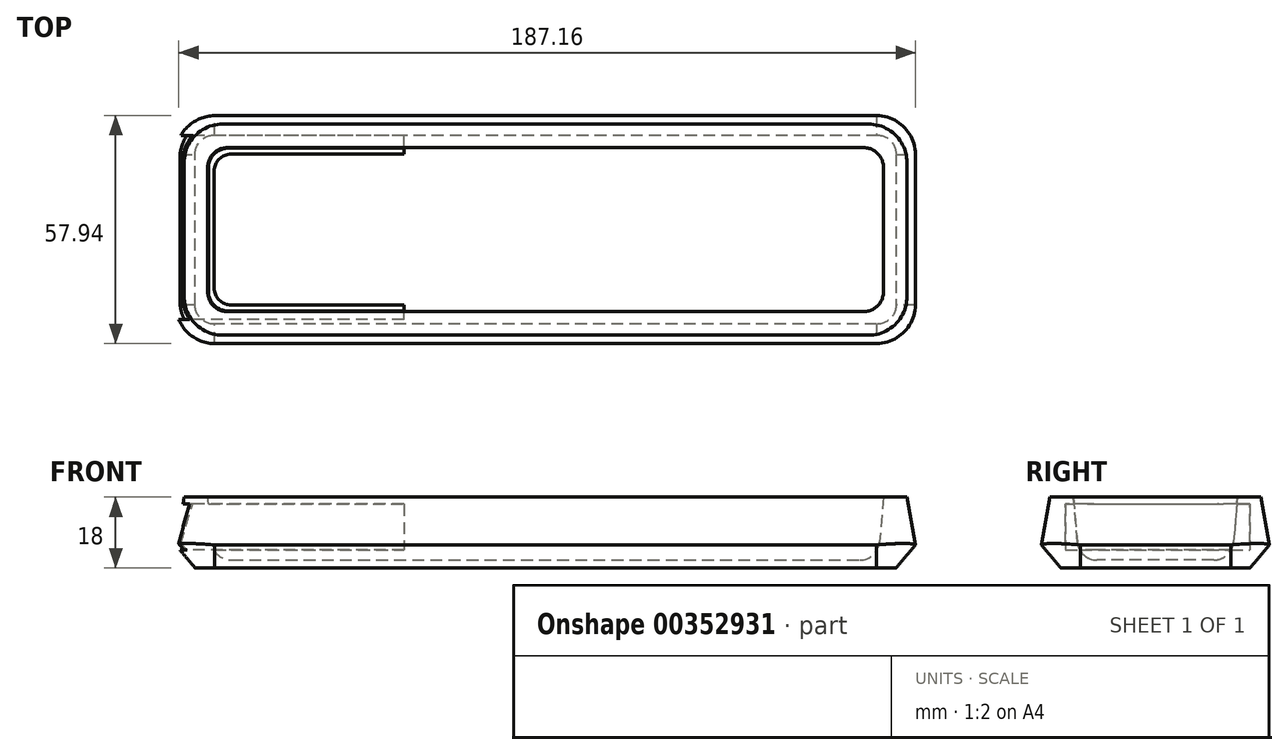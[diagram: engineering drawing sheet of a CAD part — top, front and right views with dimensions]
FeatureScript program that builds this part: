
annotation { "Feature Type Name" : "Feature", "Feature Type Description" : "" }
export const myFeature = defineFeature(function(context is Context, id is Id, definition is map)
    precondition{}
    {
        {
            var Q0;
            Q0=qCreatedBy(makeId("Top.planeOp"),FACE);
            var sketch = newSketch(context, id + "F0", { "sketchPlane" : qUnion([Q0])});
            skLineSegment(sketch, "E0.bottom", {"start": v(0, 0) * mm, "end": v(190, 0) * mm});
            skLineSegment(sketch, "E0.top", {"start": v(0, 60) * mm, "end": v(190, 60) * mm});
            skLineSegment(sketch, "E0.left", {"start": v(0, 0) * mm, "end": v(0, 60) * mm, "construction": true});
            skLineSegment(sketch, "E0.right", {"start": v(190, 0) * mm, "end": v(190, 60) * mm});
            skLineSegment(sketch, "E1", {"start": v(0, 60) * mm, "end": v(0, 0) * mm});
            skSolve(sketch);
        }
        {
            var Q0;
            Q0 = qSketchRegion(id + "F0", true);
            extrude(context, id + "F1", {"entities" : qUnion([Q0]), "depth" : 18 * mm, "hasDraft" : true, "draftAngle" : 10 * degree, "draftPullDirection" : true});
        }
        {
            var Q0;
            Q0=makeQuery(id+"F1.opExtrude","CAP_FACE",FACE,{"disambiguationData":[OSD([sQuery(id+"F0.wireOp",EDGE,"E0.bottom"),sQuery(id+"F0.wireOp",EDGE,"E0.top"),sQuery(id+"F0.wireOp",EDGE,"E0.right"),sQuery(id+"F0.wireOp",EDGE,"E1")])],"isStart":false});
            var sketch = newSketch(context, id + "F2", { "sketchPlane" : qUnion([Q0])});
            skLineSegment(sketch, "E2.bottom", {"start": v(9.17, 50.83) * mm, "end": v(180.83, 50.83) * mm});
            skLineSegment(sketch, "E2.top", {"start": v(9.17, 9.17) * mm, "end": v(180.83, 9.17) * mm});
            skLineSegment(sketch, "E2.left", {"start": v(9.17, 50.83) * mm, "end": v(9.17, 9.17) * mm});
            skLineSegment(sketch, "E2.right", {"start": v(180.83, 50.83) * mm, "end": v(180.83, 9.17) * mm});
            skSolve(sketch);
        }
        {
            var Q0;
            Q0 = qSketchRegion(id + "F2", true);
            extrude(context, id + "F3", {"entities" : qUnion([Q0]), "operationType" : NewBodyOperationType.REMOVE, "oppositeDirection" : true, "depth" : 16 * mm, "hasDraft" : true, "draftAngle" : 5 * degree, "draftPullDirection" : true});
        }
        {
            var Q0;
            Q0=makeQuery(id+"F3.boolean.opBoolean","COPY",EDGE,{"derivedFrom":makeQuery(id+"F3.opExtrude","SWEPT_EDGE",EDGE,{"disambiguationData":[OSD([sQuery(id+"F2.wireOp",EDGE,"E2.bottom"),sQuery(id+"F2.wireOp",EDGE,"E2.left")])]})});
            var Q1;
            Q1=makeQuery(id+"F3.boolean.opBoolean","COPY",EDGE,{"derivedFrom":makeQuery(id+"F3.opExtrude","SWEPT_EDGE",EDGE,{"disambiguationData":[OSD([sQuery(id+"F2.wireOp",EDGE,"E2.bottom"),sQuery(id+"F2.wireOp",EDGE,"E2.right")])]})});
            var Q2;
            Q2=makeQuery(id+"F3.boolean.opBoolean","COPY",EDGE,{"derivedFrom":makeQuery(id+"F3.opExtrude","SWEPT_EDGE",EDGE,{"disambiguationData":[OSD([sQuery(id+"F2.wireOp",EDGE,"E2.top"),sQuery(id+"F2.wireOp",EDGE,"E2.left")])]})});
            var Q3;
            Q3=makeQuery(id+"F3.boolean.opBoolean","COPY",EDGE,{"derivedFrom":makeQuery(id+"F3.opExtrude","SWEPT_EDGE",EDGE,{"disambiguationData":[OSD([sQuery(id+"F2.wireOp",EDGE,"E2.top"),sQuery(id+"F2.wireOp",EDGE,"E2.right")])]})});
            fillet(context, id + "F4", {"entities" : qUnion([Q0, Q1, Q2, Q3]), "radius" : 5 * mm, "tangentPropagation" : true, "allowEdgeOverflow" : false});
        }
        {
            var Q0;
            Q0=makeQuery(id+"F1.opExtrude","SWEPT_EDGE",EDGE,{"disambiguationData":[OSD([sQuery(id+"F0.wireOp",EDGE,"E0.bottom"),sQuery(id+"F0.wireOp",EDGE,"E0.right")])]});
            var Q1;
            Q1=makeQuery(id+"F1.opExtrude","SWEPT_EDGE",EDGE,{"disambiguationData":[OSD([sQuery(id+"F0.wireOp",EDGE,"E0.top"),sQuery(id+"F0.wireOp",EDGE,"E0.right")])]});
            var Q2;
            Q2=makeQuery(id+"F1.opExtrude","SWEPT_EDGE",EDGE,{"disambiguationData":[OSD([sQuery(id+"F0.wireOp",EDGE,"E0.bottom"),sQuery(id+"F0.wireOp",EDGE,"E1")])]});
            var Q3;
            Q3=makeQuery(id+"F1.opExtrude","SWEPT_EDGE",EDGE,{"disambiguationData":[OSD([sQuery(id+"F0.wireOp",EDGE,"E0.top"),sQuery(id+"F0.wireOp",EDGE,"E1")])]});
            fillet(context, id + "F5", {"entities" : qUnion([Q0, Q1, Q2, Q3]), "radius" : 10 * mm, "tangentPropagation" : true, "allowEdgeOverflow" : false});
        }
        {
            var Q0;
            Q0=makeQuery(id+"F3.boolean.opBoolean","COPY",EDGE,{"derivedFrom":makeQuery(id+"F3.opExtrude","CAP_EDGE",EDGE,{"disambiguationData":[OSD([sQuery(id+"F2.wireOp",EDGE,"E2.bottom")])],"isStart":false})});
            var Q1;
            Q1=makeQuery(id+"F3.boolean.opBoolean","COPY",EDGE,{"derivedFrom":makeQuery(id+"F3.opExtrude","CAP_EDGE",EDGE,{"disambiguationData":[OSD([sQuery(id+"F2.wireOp",EDGE,"E2.left")])],"isStart":false})});
            var Q2;
            Q2=makeQuery(id+"F3.boolean.opBoolean","COPY",EDGE,{"derivedFrom":makeQuery(id+"F3.opExtrude","CAP_EDGE",EDGE,{"disambiguationData":[OSD([sQuery(id+"F2.wireOp",EDGE,"E2.right")])],"isStart":false})});
            var Q3;
            Q3=makeQuery(id+"F3.boolean.opBoolean","COPY",EDGE,{"derivedFrom":makeQuery(id+"F3.opExtrude","CAP_EDGE",EDGE,{"disambiguationData":[OSD([sQuery(id+"F2.wireOp",EDGE,"E2.top")])],"isStart":false})});
            fillet(context, id + "F6", {"entities" : qUnion([Q0, Q1, Q2, Q3]), "radius" : 5 * mm, "tangentPropagation" : true, "allowEdgeOverflow" : false});
        }
        {
            var Q0;
            Q0=makeQuery(id+"F1.opExtrude","CAP_EDGE",EDGE,{"disambiguationData":[OSD([sQuery(id+"F0.wireOp",EDGE,"E0.bottom")])],"isStart":true});
            chamfer(context, id + "F7", {"entities" : qUnion([Q0]), "width" : 5 * mm, "tangentPropagation" : true});
        }
        {
            var Q0;
            Q0=qCreatedBy(makeId("Right.planeOp"),FACE);
            var sketch = newSketch(context, id + "F8", { "sketchPlane" : qUnion([Q0])});
            skLineSegment(sketch, "E3.bottom", {"start": v(7.17, 16.2) * mm, "end": v(53.93, 16.2) * mm});
            skLineSegment(sketch, "E3.top", {"start": v(7.17, 4.52) * mm, "end": v(53.93, 4.52) * mm});
            skLineSegment(sketch, "E3.left", {"start": v(7.17, 16.2) * mm, "end": v(7.17, 4.52) * mm});
            skLineSegment(sketch, "E3.right", {"start": v(53.93, 16.2) * mm, "end": v(53.93, 4.52) * mm});
            skSolve(sketch);
        }
        {
            var Q0;
            Q0 = qSketchRegion(id + "F8", true);
            extrude(context, id + "F9", {"entities" : qUnion([Q0]), "operationType" : NewBodyOperationType.REMOVE, "depth" : 59 * mm, "offsetDistance" : 25 * mm});
        }
    });
